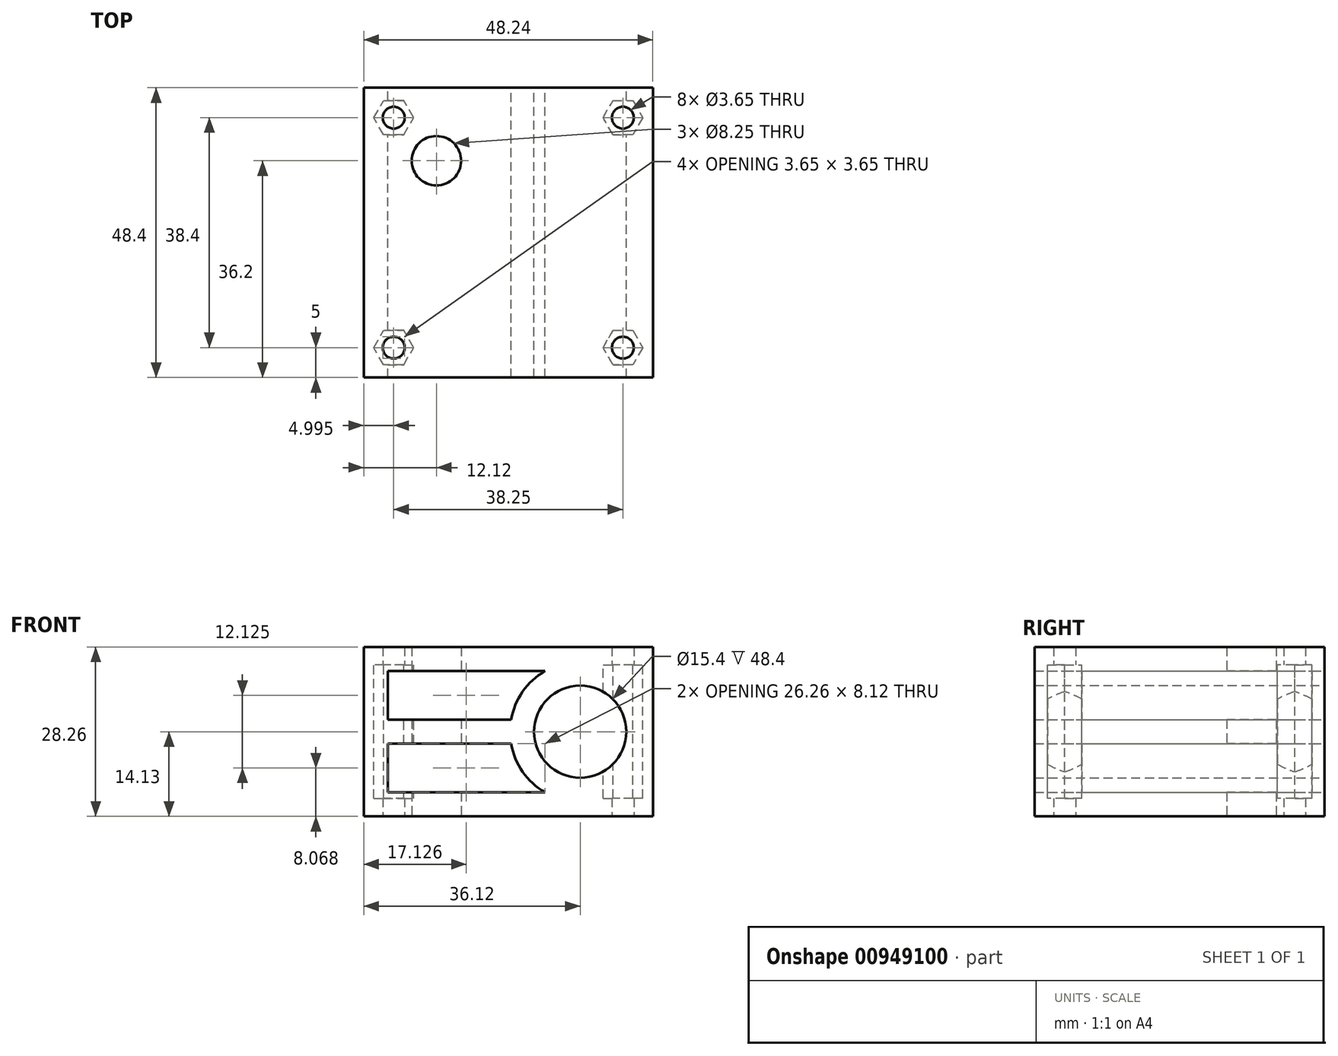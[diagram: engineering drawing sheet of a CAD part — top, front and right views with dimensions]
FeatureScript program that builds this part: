
annotation { "Feature Type Name" : "Feature", "Feature Type Description" : "" }
export const myFeature = defineFeature(function(context is Context, id is Id, definition is map)
    precondition{}
    {
        {
            assignVariable(context, id + "F0", {"name" : "border", "anyValue" : 4});
        }
        {
            assignVariable(context, id + "F1", {"name" : "tolerance_xy", "anyValue" : 0.25});
        }
        {
            assignVariable(context, id + "F2", {"name" : "tolerance_z", "anyValue" : 0.4});
        }
        {
            var Q0;
            Q0=qCreatedBy(makeId("Front.planeOp"),FACE);
            var sketch = newSketch(context, id + "F3", { "sketchPlane" : qUnion([Q0])});
            skLineSegment(sketch, "E0.bottom", {"start": v(24.12, 14.12) * mm, "end": v(-24.12, 14.12) * mm});
            skLineSegment(sketch, "E0.top", {"start": v(24.12, -14.12) * mm, "end": v(-24.12, -14.12) * mm});
            skLineSegment(sketch, "E0.left", {"start": v(24.12, 14.12) * mm, "end": v(24.12, -14.12) * mm});
            skLineSegment(sketch, "E0.right", {"start": v(-24.12, 14.12) * mm, "end": v(-24.12, -14.12) * mm});
            skPoint(sketch, "E0.middle", {"position": v(0, 0) * mm});
            skCircle(sketch, "E1", {"center": v(12, 0) * mm, "radius": 11.7 * mm});
            skCircle(sketch, "E2", {"center": v(12, 0) * mm, "radius": 7.7 * mm});
            skLineSegment(sketch, "E3.bottom", {"start": v(20.12, 10.12) * mm, "end": v(-20.12, 10.12) * mm});
            skLineSegment(sketch, "E3.top", {"start": v(20.12, -10.12) * mm, "end": v(-20.12, -10.12) * mm});
            skLineSegment(sketch, "E3.left", {"start": v(20.12, 10.12) * mm, "end": v(20.12, -10.12) * mm});
            skLineSegment(sketch, "E3.right", {"start": v(-20.12, 10.12) * mm, "end": v(-20.12, -10.12) * mm});
            skLineSegment(sketch, "E4", {"start": v(12, -10.12) * mm, "end": v(12, 10.12) * mm, "construction": true});
            skLineSegment(sketch, "E5", {"start": v(-20.12, 0) * mm, "end": v(20.12, 0) * mm, "construction": true});
            skLineSegment(sketch, "E6", {"start": v(0.47, 2) * mm, "end": v(-20.12, 2) * mm});
            skLineSegment(sketch, "E7", {"start": v(0.47, -2) * mm, "end": v(-20.12, -2) * mm});
            skLineSegment(sketch, "E8", {"start": v(10, 10.12) * mm, "end": v(10, 11.53) * mm});
            skLineSegment(sketch, "E9", {"start": v(14, 10.12) * mm, "end": v(14, 11.53) * mm});
            skLineSegment(sketch, "E10", {"start": v(10, -10.12) * mm, "end": v(10, -11.53) * mm});
            skLineSegment(sketch, "E11", {"start": v(14, -10.12) * mm, "end": v(14, -11.53) * mm});
            skLineSegment(sketch, "E12", {"start": v(23.53, 2) * mm, "end": v(20.12, 2) * mm});
            skLineSegment(sketch, "E13", {"start": v(23.53, -2) * mm, "end": v(20.12, -2) * mm});
            skSolve(sketch);
        }
        {
            var Q0;
            Q0=makeQuery(id+"F3.imprint","IMPRINT",FACE,{"disambiguationData":[TD([[makeQuery(id+"F3.imprint","IMPRINT",EDGE,{"derivedFrom":sQuery(id+"F3.wireOp",EDGE,"E0.bottom")}),1.0]])]});
            var Q1;
            {var subQ0=sQuery(id+"F3.wireOp",EDGE,"E8");Q1=makeQuery(id+"F3.imprint","IMPRINT",FACE,{"disambiguationData":[TD([[makeQuery(id+"F3.imprint","IMPRINT",EDGE,{"derivedFrom":subQ0}),-1.0]])]});}
            var Q2;
            Q2=makeQuery(id+"F3.imprint","IMPRINT",FACE,{"disambiguationData":[TD([[makeQuery(id+"F3.imprint","IMPRINT",EDGE,{"derivedFrom":sQuery(id+"F3.wireOp",EDGE,"E2")}),-1.0]])]});
            var Q3;
            {var subQ0=sQuery(id+"F3.wireOp",EDGE,"E10");Q3=makeQuery(id+"F3.imprint","IMPRINT",FACE,{"disambiguationData":[TD([[makeQuery(id+"F3.imprint","IMPRINT",EDGE,{"derivedFrom":subQ0}),1.0]])]});}
            var Q4;
            {var subQ0=sQuery(id+"F3.wireOp",EDGE,"E6");Q4=makeQuery(id+"F3.imprint","IMPRINT",FACE,{"disambiguationData":[TD([[makeQuery(id+"F3.imprint","IMPRINT",EDGE,{"derivedFrom":subQ0}),1.0]])]});}
            var Q5;
            {var subQ0=sQuery(id+"F3.wireOp",EDGE,"E12");Q5=makeQuery(id+"F3.imprint","IMPRINT",FACE,{"disambiguationData":[TD([[makeQuery(id+"F3.imprint","IMPRINT",EDGE,{"derivedFrom":subQ0}),1.0]])]});}
            var Q6;
            {var subQ0=sQuery(id+"F3.wireOp",EDGE,"E12");Q6=makeQuery(id+"F3.imprint","IMPRINT",FACE,{"disambiguationData":[TD([[makeQuery(id+"F3.imprint","IMPRINT",EDGE,{"derivedFrom":subQ0}),-1.0]])]});}
            var Q7;
            {var subQ0=sQuery(id+"F3.wireOp",EDGE,"E13");Q7=makeQuery(id+"F3.imprint","IMPRINT",FACE,{"disambiguationData":[TD([[makeQuery(id+"F3.imprint","IMPRINT",EDGE,{"derivedFrom":subQ0}),1.0]])]});}
            var Q8;
            {var subQ0=sQuery(id+"F3.wireOp",EDGE,"xwtNpsUs-C44z-uagX-IKFE-Rp0NLuXpZdO7");Q8=makeQuery(id+"F3.imprint","IMPRINT",FACE,{"disambiguationData":[TD([[makeQuery(id+"F3.imprint","IMPRINT",EDGE,{"derivedFrom":subQ0}),-1.0]])]});}
            var Q9;
            {var subQ3=sQuery(id+"F3.wireOp",EDGE,"iiPWomU2-JPy6-PKDB-MISC-S4ZnLnR1PTqr");Q9=makeQuery(id+"F3.imprint","IMPRINT",FACE,{"disambiguationData":[TD([[makeQuery(id+"F3.imprint","IMPRINT",EDGE,{"derivedFrom":subQ3}),-1.0]])]});}
            var Q10;
            {var subQ0=sQuery(id+"F3.wireOp",EDGE,"E9");Q10=makeQuery(id+"F3.imprint","IMPRINT",FACE,{"disambiguationData":[TD([[makeQuery(id+"F3.imprint","IMPRINT",EDGE,{"derivedFrom":subQ0}),-1.0]])]});}
            var Q11;
            {var subQ0=sQuery(id+"F3.wireOp",EDGE,"E8");Q11=makeQuery(id+"F3.imprint","IMPRINT",FACE,{"disambiguationData":[TD([[makeQuery(id+"F3.imprint","IMPRINT",EDGE,{"derivedFrom":subQ0}),1.0]])]});}
            var Q12;
            {var subQ0=sQuery(id+"F3.wireOp",EDGE,"E3.left");var subQ1=sQuery(id+"F3.wireOp",EDGE,"E1");var subQ2=makeQuery(id+"F3.imprint","INTERSECT",VERTEX,{"disambiguationData":[OD(0.0)],"derivedFrom":[subQ1,subQ0]});Q12=makeQuery(id+"F3.imprint","IMPRINT",FACE,{"disambiguationData":[TD([[makeQuery(id+"F3.imprint","IMPRINT",EDGE,{"disambiguationData":[TD([[subQ2,-1.0]])],"derivedFrom":subQ1}),-1.0]])]});}
            var Q13;
            {var subQ0=sQuery(id+"F3.wireOp",EDGE,"E3.top");var subQ1=sQuery(id+"F3.wireOp",EDGE,"E1");var subQ2=makeQuery(id+"F3.imprint","INTERSECT",VERTEX,{"disambiguationData":[OD(1.0)],"derivedFrom":[subQ1,subQ0]});Q13=makeQuery(id+"F3.imprint","IMPRINT",FACE,{"disambiguationData":[TD([[makeQuery(id+"F3.imprint","IMPRINT",EDGE,{"disambiguationData":[TD([[subQ2,-1.0]])],"derivedFrom":subQ1}),-1.0]])]});}
            var Q14;
            {var subQ0=sQuery(id+"F3.wireOp",EDGE,"E11");Q14=makeQuery(id+"F3.imprint","IMPRINT",FACE,{"disambiguationData":[TD([[makeQuery(id+"F3.imprint","IMPRINT",EDGE,{"derivedFrom":subQ0}),1.0]])]});}
            var Q15;
            {var subQ0=sQuery(id+"F3.wireOp",EDGE,"E10");Q15=makeQuery(id+"F3.imprint","IMPRINT",FACE,{"disambiguationData":[TD([[makeQuery(id+"F3.imprint","IMPRINT",EDGE,{"derivedFrom":subQ0}),-1.0]])]});}
            extrude(context, id + "F4", {"entities" : qUnion([Q0, Q1, Q2, Q3, Q4, Q5, Q6, Q7, Q8, Q9, Q10, Q11, Q12, Q13, Q14, Q15]), "endBound" : BoundingType.SYMMETRIC, "depth" : (48 + getVariable(context, 'tolerance_z')) * mm, "offsetDistance" : 25 * mm});
        }
        {
            var Q0;
            Q0=makeQuery(id+"F4.opExtrude","SWEPT_FACE",FACE,{"disambiguationData":[OSD([sQuery(id+"F3.wireOp",EDGE,"E0.top")])]});
            var sketch = newSketch(context, id + "F5", { "sketchPlane" : qUnion([Q0])});
            skLineSegment(sketch, "E14.0", {"start": v(24.12, 24.2) * mm, "end": v(-24.12, 24.2) * mm});
            skLineSegment(sketch, "E14.1", {"start": v(-24.12, 24.2) * mm, "end": v(-24.12, -24.2) * mm});
            skLineSegment(sketch, "E14.3", {"start": v(24.12, -24.2) * mm, "end": v(-24.12, -24.2) * mm});
            skLineSegment(sketch, "E14.4", {"start": v(24.12, 24.2) * mm, "end": v(24.12, -24.2) * mm});
            skCircle(sketch, "E15", {"center": v(-19.12, 19.2) * mm, "radius": 1.82 * mm});
            skCircle(sketch, "E16", {"center": v(19.12, 19.2) * mm, "radius": 1.82 * mm});
            skCircle(sketch, "E17", {"center": v(19.12, -19.2) * mm, "radius": 1.82 * mm});
            skCircle(sketch, "E18", {"center": v(-19.12, -19.2) * mm, "radius": 1.82 * mm});
            skLineSegment(sketch, "E19", {"start": v(0, 24.2) * mm, "end": v(0, -24.2) * mm, "construction": true});
            skLineSegment(sketch, "E20", {"start": v(-24.12, 0) * mm, "end": v(24.12, 0) * mm, "construction": true});
            skCircle(sketch, "E21", {"center": v(-12, -12) * mm, "radius": 4.12 * mm});
            skSolve(sketch);
        }
        {
            var Q0;
            Q0=makeQuery(id+"F5.imprint","IMPRINT",FACE,{"disambiguationData":[TD([[makeQuery(id+"F5.imprint","IMPRINT",EDGE,{"derivedFrom":sQuery(id+"F5.wireOp",EDGE,"E15")}),1.0]])]});
            var Q1;
            Q1=makeQuery(id+"F5.imprint","IMPRINT",FACE,{"disambiguationData":[TD([[makeQuery(id+"F5.imprint","IMPRINT",EDGE,{"derivedFrom":sQuery(id+"F5.wireOp",EDGE,"E16")}),1.0]])]});
            var Q2;
            Q2=makeQuery(id+"F5.imprint","IMPRINT",FACE,{"disambiguationData":[TD([[makeQuery(id+"F5.imprint","IMPRINT",EDGE,{"derivedFrom":sQuery(id+"F5.wireOp",EDGE,"E17")}),1.0]])]});
            var Q3;
            Q3=makeQuery(id+"F5.imprint","IMPRINT",FACE,{"disambiguationData":[TD([[makeQuery(id+"F5.imprint","IMPRINT",EDGE,{"derivedFrom":sQuery(id+"F5.wireOp",EDGE,"E18")}),1.0]])]});
            extrude(context, id + "F6", {"entities" : qUnion([Q0, Q1, Q2, Q3]), "operationType" : NewBodyOperationType.REMOVE, "oppositeDirection" : true, "depth" : (28 + getVariable(context, 'tolerance_xy')) * mm, "offsetDistance" : 25 * mm});
        }
        {
            var Q0;
            Q0=makeQuery(id+"F5.imprint","IMPRINT",FACE,{"disambiguationData":[TD([[makeQuery(id+"F5.imprint","IMPRINT",EDGE,{"derivedFrom":sQuery(id+"F5.wireOp",EDGE,"E21")}),1.0]])]});
            extrude(context, id + "F7", {"entities" : qUnion([Q0]), "operationType" : NewBodyOperationType.REMOVE, "oppositeDirection" : true, "depth" : (28 + getVariable(context, 'tolerance_xy')) * mm, "offsetDistance" : 25 * mm});
        }
        {
            var Q0;
            Q0=makeQuery(id+"F4.opExtrude","SWEPT_FACE",FACE,{"disambiguationData":[OSD([sQuery(id+"F3.wireOp",EDGE,"E6")])]});
            var sketch = newSketch(context, id + "F8", { "sketchPlane" : qUnion([Q0])});
            skLineSegment(sketch, "E22.0", {"start": v(24.12, 24.2) * mm, "end": v(-24.12, 24.2) * mm, "construction": true});
            skLineSegment(sketch, "E22.1", {"start": v(24.12, -24.2) * mm, "end": v(24.12, 24.2) * mm, "construction": true});
            skLineSegment(sketch, "E22.2", {"start": v(-24.12, -24.2) * mm, "end": v(-24.12, 24.2) * mm, "construction": true});
            skLineSegment(sketch, "E22.3", {"start": v(24.12, -24.2) * mm, "end": v(-24.12, -24.2) * mm, "construction": true});
            skCircle(sketch, "E23.0", {"center": v(-19.12, -19.2) * mm, "radius": 1.83 * mm, "construction": true});
            skCircle(sketch, "E23.1", {"center": v(19.12, -19.2) * mm, "radius": 1.83 * mm, "construction": true});
            skCircle(sketch, "E23.2", {"center": v(-19.12, 19.2) * mm, "radius": 1.83 * mm, "construction": true});
            skCircle(sketch, "E23.3", {"center": v(19.12, 19.2) * mm, "radius": 1.83 * mm, "construction": true});
            skCircle(sketch, "E24.cCircle", {"center": v(19.12, -19.2) * mm, "radius": 2.88 * mm, "construction": true});
            skLineSegment(sketch, "E24.0", {"start": v(17.47, -16.32) * mm, "end": v(20.78, -16.32) * mm});
            skLineSegment(sketch, "E24.1", {"start": v(20.78, -16.33) * mm, "end": v(22.44, -19.2) * mm});
            skLineSegment(sketch, "E24.2", {"start": v(22.44, -19.2) * mm, "end": v(20.78, -22.07) * mm});
            skLineSegment(sketch, "E24.3", {"start": v(20.78, -22.07) * mm, "end": v(17.47, -22.07) * mm});
            skLineSegment(sketch, "E24.4", {"start": v(17.47, -22.08) * mm, "end": v(15.8, -19.2) * mm});
            skLineSegment(sketch, "E24.5", {"start": v(15.8, -19.2) * mm, "end": v(17.47, -16.33) * mm});
            skPoint(sketch, "E24.0.midPoint", {"position": v(19.12, -16.32) * mm});
            skCircle(sketch, "E25.cCircle", {"center": v(19.12, 19.2) * mm, "radius": 2.88 * mm, "construction": true});
            skLineSegment(sketch, "E25.0", {"start": v(20.78, 16.32) * mm, "end": v(17.47, 16.32) * mm});
            skLineSegment(sketch, "E25.1", {"start": v(17.47, 16.32) * mm, "end": v(15.8, 19.2) * mm});
            skLineSegment(sketch, "E25.2", {"start": v(15.8, 19.2) * mm, "end": v(17.47, 22.07) * mm});
            skLineSegment(sketch, "E25.3", {"start": v(17.47, 22.07) * mm, "end": v(20.78, 22.07) * mm});
            skLineSegment(sketch, "E25.4", {"start": v(20.78, 22.07) * mm, "end": v(22.44, 19.2) * mm});
            skLineSegment(sketch, "E25.5", {"start": v(22.44, 19.2) * mm, "end": v(20.78, 16.32) * mm});
            skPoint(sketch, "E25.0.midPoint", {"position": v(19.12, 16.32) * mm});
            skCircle(sketch, "E26.cCircle", {"center": v(-19.12, 19.2) * mm, "radius": 2.88 * mm, "construction": true});
            skLineSegment(sketch, "E26.0", {"start": v(-17.47, 16.32) * mm, "end": v(-20.78, 16.32) * mm});
            skLineSegment(sketch, "E26.1", {"start": v(-20.78, 16.32) * mm, "end": v(-22.44, 19.2) * mm});
            skLineSegment(sketch, "E26.2", {"start": v(-22.44, 19.2) * mm, "end": v(-20.78, 22.07) * mm});
            skLineSegment(sketch, "E26.3", {"start": v(-20.78, 22.07) * mm, "end": v(-17.47, 22.07) * mm});
            skLineSegment(sketch, "E26.4", {"start": v(-17.47, 22.07) * mm, "end": v(-15.8, 19.2) * mm});
            skLineSegment(sketch, "E26.5", {"start": v(-15.8, 19.2) * mm, "end": v(-17.47, 16.32) * mm});
            skPoint(sketch, "E26.0.midPoint", {"position": v(-19.12, 16.32) * mm});
            skCircle(sketch, "E27.cCircle", {"center": v(-19.12, -19.2) * mm, "radius": 2.88 * mm, "construction": true});
            skLineSegment(sketch, "E27.0", {"start": v(-20.78, -16.32) * mm, "end": v(-17.47, -16.32) * mm});
            skLineSegment(sketch, "E27.1", {"start": v(-17.47, -16.32) * mm, "end": v(-15.8, -19.2) * mm});
            skLineSegment(sketch, "E27.2", {"start": v(-15.8, -19.2) * mm, "end": v(-17.47, -22.07) * mm});
            skLineSegment(sketch, "E27.3", {"start": v(-17.47, -22.07) * mm, "end": v(-20.78, -22.07) * mm});
            skLineSegment(sketch, "E27.4", {"start": v(-20.78, -22.08) * mm, "end": v(-22.44, -19.2) * mm});
            skLineSegment(sketch, "E27.5", {"start": v(-22.44, -19.2) * mm, "end": v(-20.78, -16.32) * mm});
            skPoint(sketch, "E27.0.midPoint", {"position": v(-19.12, -16.32) * mm});
            skSolve(sketch);
        }
        {
            var Q0;
            Q0 = qSketchRegion(id + "F8", true);
            extrude(context, id + "F9", {"entities" : qUnion([Q0]), "operationType" : NewBodyOperationType.REMOVE, "oppositeDirection" : true, "depth" : (((28 + getVariable(context, 'tolerance_xy')) / 2) - 1 / 2 * getVariable(context, 'border') + 1) * mm, "offsetDistance" : 25 * mm, "hasSecondDirection" : true, "secondDirectionOppositeDirection" : false, "secondDirectionDepth" : (((28 + getVariable(context, 'tolerance_xy')) / 2) - 3 / 2 * getVariable(context, 'border') + 1) * mm});
        }
    });
